# Revit family: Zumtobel KAVA LED
name_source: partatom
category: Lighting Fixtures
revit_build: Autodesk Revit 2014 (Build: 20140709_2115(x64)
units: mm (PartAtom-declared; Revit-internal decimal feet)

## types (2) — shared parameters
Assembly Code = D5020200
Body = Zumtobel_Metal_Aluminium
Color Filter = 16777215
Cover = Zumtobel_PMMA_Self_llumination_Opaque
Description = KAVA LED
Dimming Lamp Color Temperature Shift = <None>
Emit Shape Visible in Rendering = Yes
Lamp = LED
Manufacturer = Zumtobel Lighting
Model = 60816404
Tilt Angle = 90.00°
URL = http://www.zumtobel.com
Voltage = 230 V
zero-valued in all types: Default Elevation

## per-type parameters (varying)
| type | 122 Width | 240 Width | Apparent Load | Emit from Rectangle Length | Emit from Rectangle Width | Frame Width | Height | Length | Photometric Web File | Width |
| KAVA Q110 LED70-840 24V SRE | Yes | No | 1 VA | 112 mm | 112 mm | 10 mm  [stored 0.0328084 ft] | 47 mm  [stored 0.154199 ft] | 122 mm  [stored 0.400262 ft] | 60816404_(STD).IES | 122 mm  [stored 0.400262 ft] |
| KAVA Q220 LED600-840 24V SRE | No | Yes | 11 VA | 226 mm  [stored 0.74147 ft] | 226 mm  [stored 0.74147 ft] | 14 mm  [stored 0.0459318 ft] | 79 mm | 240 mm  [stored 0.787402 ft] | 60816407_(STD).IES | 240 mm  [stored 0.787402 ft] |

note: [stored X ft] marks values corroborated as IEEE doubles in the binary element streams (Revit-internal decimal feet)

## geometry (parser evidence)
native form markers: Sweep x2
no freeform markers — native parametric forms only
